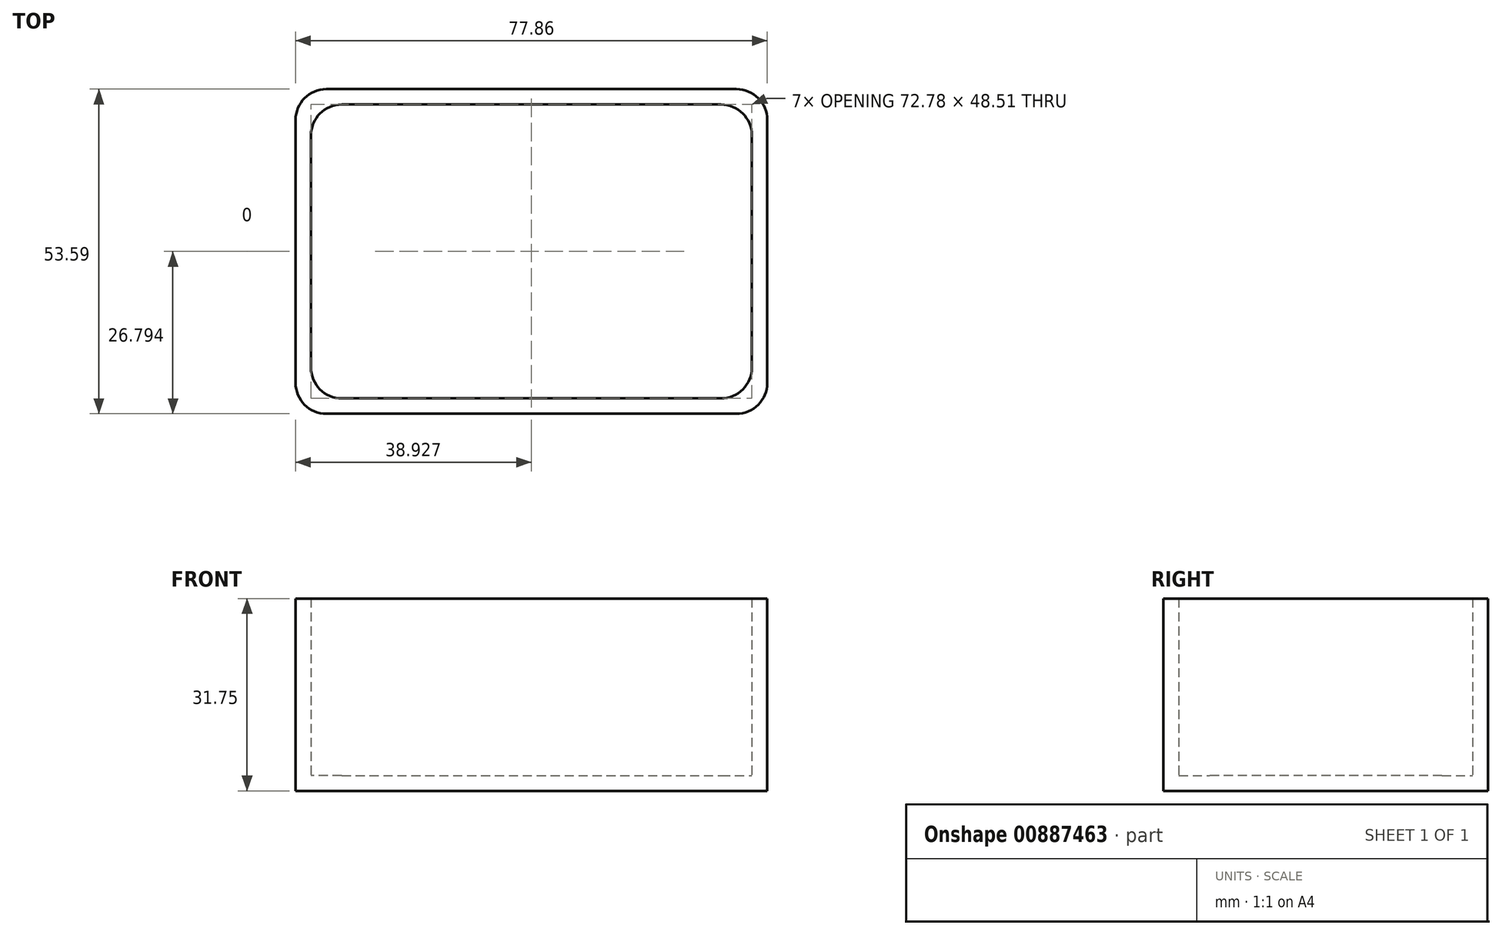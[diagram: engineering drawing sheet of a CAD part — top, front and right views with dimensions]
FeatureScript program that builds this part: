
annotation { "Feature Type Name" : "Feature", "Feature Type Description" : "" }
export const myFeature = defineFeature(function(context is Context, id is Id, definition is map)
    precondition{}
    {
        {
            var Q0;
            Q0=qCreatedBy(makeId("Top.planeOp"),FACE);
            var sketch = newSketch(context, id + "F0", { "sketchPlane" : qUnion([Q0])});
            skLineSegment(sketch, "E0.bottom", {"start": v(1.9, 0) * mm, "end": v(79.76, 0) * mm});
            skLineSegment(sketch, "E0.top", {"start": v(1.9, -53.6) * mm, "end": v(79.76, -53.6) * mm});
            skLineSegment(sketch, "E0.left", {"start": v(1.9, 0) * mm, "end": v(1.9, -53.6) * mm});
            skLineSegment(sketch, "E0.right", {"start": v(79.76, 0) * mm, "end": v(79.76, -53.6) * mm});
            skSolve(sketch);
        }
        {
            var Q0;
            Q0 = qSketchRegion(id + "F0", true);
            var Q1;
            Q1=makeQuery(id+"F0.imprint","IMPRINT",FACE,{"disambiguationData":[TD([[makeQuery(id+"F0.imprint","IMPRINT",EDGE,{"derivedFrom":sQuery(id+"F0.wireOp",EDGE,"E0.bottom")}),-1.0]])]});
            extrude(context, id + "F1", {"entities" : qUnion([Q0, Q1]), "depth" : 31.75 * mm, "offsetDistance" : 25.4 * mm});
        }
        {
            var Q0;
            Q0=makeQuery(id+"F1.opExtrude","CAP_FACE",FACE,{"disambiguationData":[OSD([sQuery(id+"F0.wireOp",EDGE,"E0.bottom"),sQuery(id+"F0.wireOp",EDGE,"E0.top"),sQuery(id+"F0.wireOp",EDGE,"E0.left"),sQuery(id+"F0.wireOp",EDGE,"E0.right")])],"isStart":false});
            shell(context, id + "F2", {"entities" : qUnion([Q0]), "thickness" : 2.54 * mm});
        }
        {
            var Q0;
            Q0=makeQuery(id+"F1.opExtrude","SWEPT_EDGE",EDGE,{"disambiguationData":[OSD([sQuery(id+"F0.wireOp",EDGE,"E0.bottom"),sQuery(id+"F0.wireOp",EDGE,"E0.left")])]});
            var Q1;
            Q1=makeQuery(id+"F1.opExtrude","SWEPT_EDGE",EDGE,{"disambiguationData":[OSD([sQuery(id+"F0.wireOp",EDGE,"E0.bottom"),sQuery(id+"F0.wireOp",EDGE,"E0.right")])]});
            var Q2;
            Q2=makeQuery(id+"F1.opExtrude","SWEPT_EDGE",EDGE,{"disambiguationData":[OSD([sQuery(id+"F0.wireOp",EDGE,"E0.top"),sQuery(id+"F0.wireOp",EDGE,"E0.right")])]});
            var Q3;
            Q3=makeQuery(id+"F1.opExtrude","SWEPT_EDGE",EDGE,{"disambiguationData":[OSD([sQuery(id+"F0.wireOp",EDGE,"E0.top"),sQuery(id+"F0.wireOp",EDGE,"E0.left")])]});
            var Q4;
            Q4=makeQuery(id+"F2.opShell","OFFSET_EDGE",EDGE,{"disambiguationData":[OSD([sQuery(id+"F0.wireOp",EDGE,"E0.top"),sQuery(id+"F0.wireOp",EDGE,"E0.left")])]});
            var Q5;
            Q5=makeQuery(id+"F2.opShell","OFFSET_EDGE",EDGE,{"disambiguationData":[OSD([sQuery(id+"F0.wireOp",EDGE,"E0.bottom"),sQuery(id+"F0.wireOp",EDGE,"E0.left")])]});
            var Q6;
            Q6=makeQuery(id+"F2.opShell","OFFSET_EDGE",EDGE,{"disambiguationData":[OSD([sQuery(id+"F0.wireOp",EDGE,"E0.bottom"),sQuery(id+"F0.wireOp",EDGE,"E0.right")])]});
            var Q7;
            Q7=makeQuery(id+"F2.opShell","OFFSET_EDGE",EDGE,{"disambiguationData":[OSD([sQuery(id+"F0.wireOp",EDGE,"E0.top"),sQuery(id+"F0.wireOp",EDGE,"E0.right")])]});
            fillet(context, id + "F3", {"entities" : qUnion([Q0, Q1, Q2, Q3, Q4, Q5, Q6, Q7]), "radius" : 5.08 * mm, "tangentPropagation" : true, "allowEdgeOverflow" : false});
        }
    });
